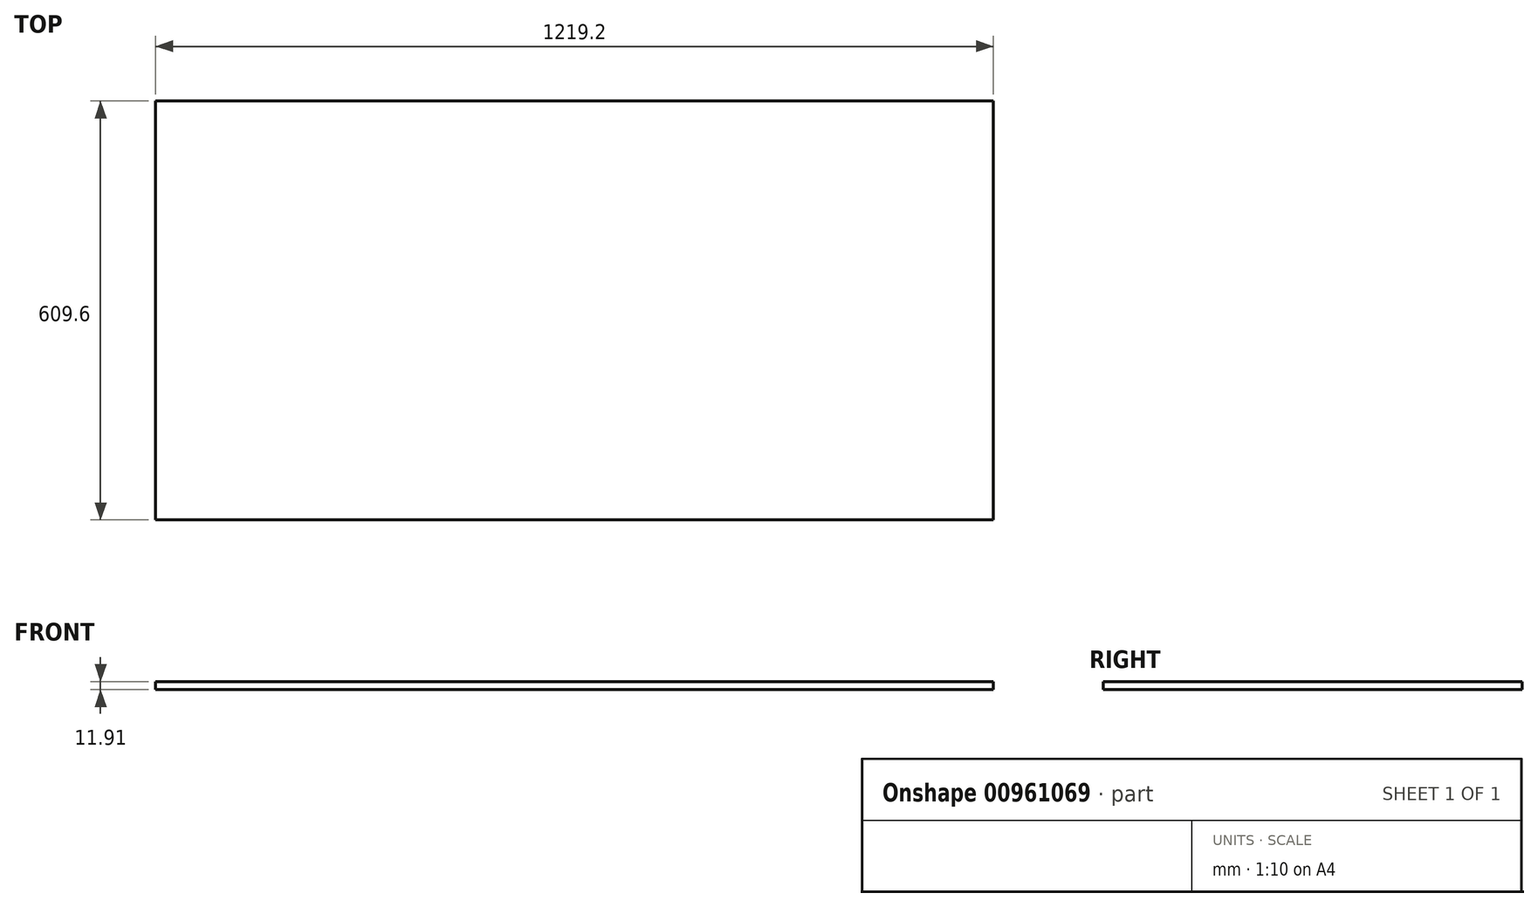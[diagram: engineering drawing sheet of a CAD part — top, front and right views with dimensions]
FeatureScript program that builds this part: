
annotation { "Feature Type Name" : "Feature", "Feature Type Description" : "" }
export const myFeature = defineFeature(function(context is Context, id is Id, definition is map)
    precondition{}
    {
        {
            var Q0;
            Q0=qCreatedBy(makeId("Front.planeOp"),FACE);
            var sketch = newSketch(context, id + "F0", { "sketchPlane" : qUnion([Q0])});
            skLineSegment(sketch, "E0.bottom", {"start": v(-366.63, 36.44) * mm, "end": v(852.57, 36.44) * mm});
            skLineSegment(sketch, "E0.top", {"start": v(-366.63, 48.35) * mm, "end": v(852.57, 48.35) * mm});
            skLineSegment(sketch, "E0.left", {"start": v(-366.63, 36.44) * mm, "end": v(-366.63, 48.35) * mm});
            skLineSegment(sketch, "E0.right", {"start": v(852.57, 36.44) * mm, "end": v(852.57, 48.35) * mm});
            skLineSegment(sketch, "E1.bottom", {"start": v(-1762, 47.6) * mm, "end": v(-542.8, 47.6) * mm});
            skLineSegment(sketch, "E1.top", {"start": v(-1762, 59.5) * mm, "end": v(-542.8, 59.5) * mm});
            skLineSegment(sketch, "E1.left", {"start": v(-1762, 47.6) * mm, "end": v(-1762, 59.5) * mm});
            skLineSegment(sketch, "E1.right", {"start": v(-542.8, 47.6) * mm, "end": v(-542.8, 59.5) * mm});
            skSolve(sketch);
        }
        {
            var Q0;
            Q0=makeQuery(id+"F0.imprint","IMPRINT",FACE,{"disambiguationData":[TD([[makeQuery(id+"F0.imprint","IMPRINT",EDGE,{"derivedFrom":sQuery(id+"F0.wireOp",EDGE,"E0.bottom")}),1.0]])]});
            extrude(context, id + "F1", {"entities" : qUnion([Q0]), "depth" : 609.6 * mm, "offsetDistance" : 25.4 * mm});
        }
    });
